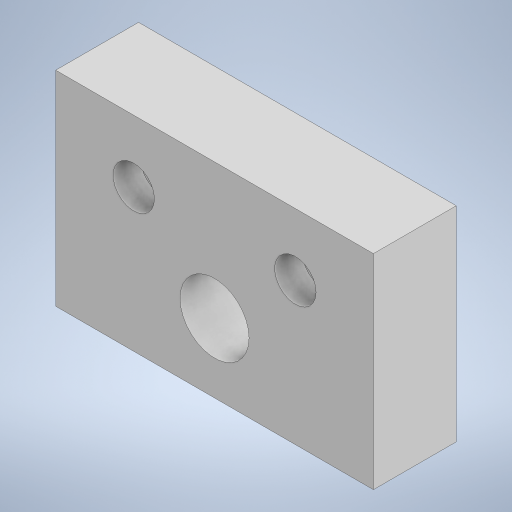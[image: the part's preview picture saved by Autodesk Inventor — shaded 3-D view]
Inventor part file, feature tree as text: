
AUTODESK INVENTOR PART (.ipt)
format: ipt  version: 2023 (Build 270158000, 158)  size: 212,480 bytes
history: native  units: in
note: dims shown in document units (in); Inventor stores cm internally (conversion verified against a paired STEP export)
features: extrude x2, sketch x2
ambient origin geometry x8: Origin, YZ Plane, XZ Plane, XY Plane, X Axis, Y Axis, Z Axis, Center Point
bodies: Solid1 (feature_tree)
feature tree (4):
  extrude  "Extrusion1"  Depth=0.5827in
  extrude  "Extrusion2"  Depth=0.1575in
  sketch  "Sketch1"  dims[d0=0.9055in d1=0.5827in]
  sketch  "Sketch2"  dims[d2=0.1772in d3=0.4606in d4=0.2224in d5=0.2224in d6=0.4528in d7=0.1969in d8=0.1181in d9=0.1181in d10=0.1969in d11=0.2362in d12=0.0in d13=0.1969in d14=0.1969in d15=0.1575in d16=0.0in]
